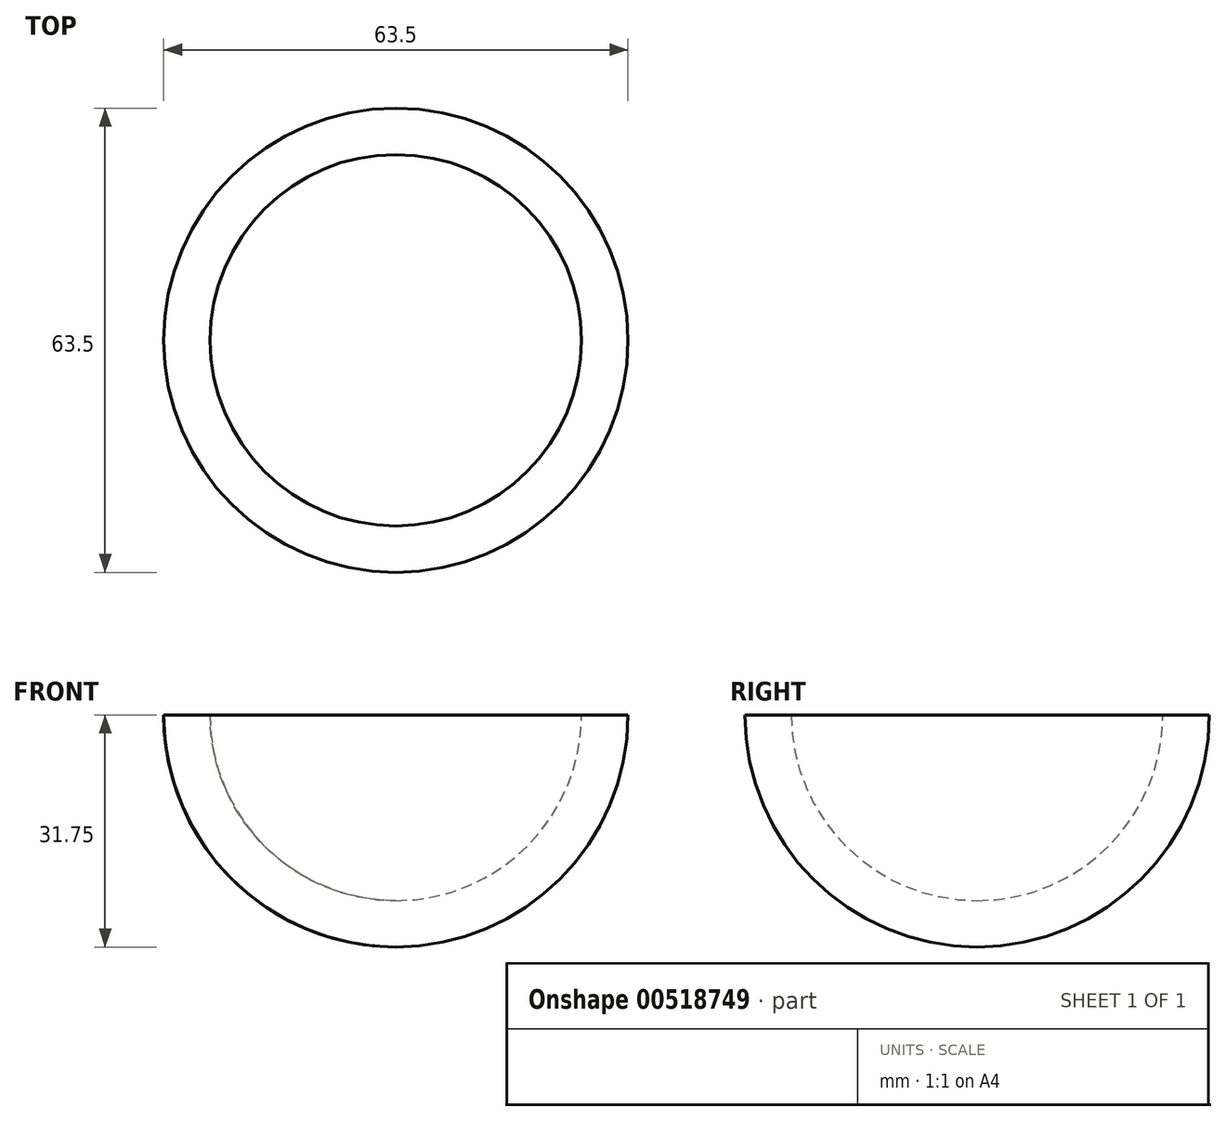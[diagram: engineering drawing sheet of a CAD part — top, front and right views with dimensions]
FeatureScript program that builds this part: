
annotation { "Feature Type Name" : "Feature", "Feature Type Description" : "" }
export const myFeature = defineFeature(function(context is Context, id is Id, definition is map)
    precondition{}
    {
        {
            var Q0;
            Q0=qCreatedBy(makeId("Front.planeOp"),FACE);
            var sketch = newSketch(context, id + "F0", { "sketchPlane" : qUnion([Q0])});
            skArc(sketch, "E0", {"start": v(-25.4, 0) * mm, "mid": v(0, -25.4) * mm, "end": v(25.4, 0) * mm});
            skArc(sketch, "E1", {"start": v(-31.75, 0) * mm, "mid": v(0, -31.75) * mm, "end": v(31.75, 0) * mm});
            skLineSegment(sketch, "E2", {"start": v(-31.75, 0) * mm, "end": v(-25.4, 0) * mm});
            skLineSegment(sketch, "E3.trimOffspring", {"start": v(25.4, 0) * mm, "end": v(31.75, 0) * mm});
            skLineSegment(sketch, "E4", {"start": v(0, -25.4) * mm, "end": v(0, -31.75) * mm});
            skSolve(sketch);
        }
        {
            var Q0;
            {var subQ0=sQuery(id+"F0.wireOp",EDGE,"E2");Q0=makeQuery(id+"F0.imprint","IMPRINT",FACE,{"disambiguationData":[TD([[makeQuery(id+"F0.imprint","IMPRINT",EDGE,{"derivedFrom":subQ0}),-1.0]])]});}
            var Q1;
            Q1=sQuery(id+"F0.wireOp",EDGE,"E4");
            revolve(context, id + "F1", {"entities" : qUnion([Q0]), "axis" : qUnion([Q1]), "revolveType" : RevolveType.FULL});
        }
    });
